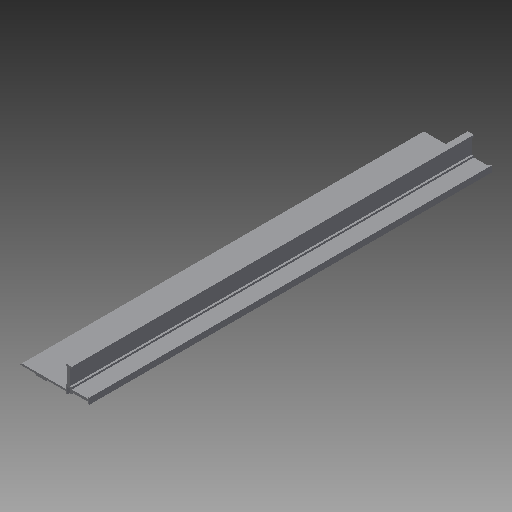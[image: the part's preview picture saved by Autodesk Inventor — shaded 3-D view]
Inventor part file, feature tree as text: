
AUTODESK INVENTOR PART (.ipt)
format: ipt  version: 2018 (Build 220112000, 112)  size: 136,192 bytes
history: native  units: mm
features: other x63, extrude x1, sketch x1
ambient origin geometry x8: Origin, YZ Plane, XZ Plane, XY Plane, X Axis, Y Axis, Z Axis, Center Point
bodies: Solid1 (feature_tree)
feature tree (65):
  extrude  "Extrusion1"  [1 undecoded]
  other  "start_XY"
  other  "start_YZ"
  other  "start_ZX"
  other  "start_X"
  other  "start_Y"
  other  "start_Z"
  other  "start_Center"
  other  "end_XY"
  other  "end_YZ"
  other  "end_ZX"
  other  "end_X"
  other  "end_Y"
  other  "end_Z"
  other  "end_Center"
  other  "side_1a_XY"
  other  "side_1a_YZ"
  other  "side_1a_ZX"
  other  "side_1a_X"
  other  "side_1a_Y"
  other  "side_1a_Z"
  other  "side_1a_Center"
  other  "side_1b_XY"
  other  "side_1b_YZ"
  other  "side_1b_ZX"
  other  "side_1b_X"
  other  "side_1b_Y"
  other  "side_1b_Z"
  other  "side_1b_Center"
  other  "side_1_XY"
  other  "side_1_YZ"
  other  "side_1_ZX"
  other  "side_1_X"
  other  "side_1_Y"
  other  "side_1_Z"
  other  "side_1_Center"
  other  "side_6a_XY"
  other  "side_6a_YZ"
  other  "side_6a_ZX"
  other  "side_6a_X"
  other  "side_6a_Y"
  other  "side_6a_Z"
  other  "side_6a_Center"
  other  "side_2_XY"
  other  "side_2_YZ"
  other  "side_2_ZX"
  other  "side_2_X"
  other  "side_2_Y"
  other  "side_2_Z"
  other  "side_2_Center"
  other  "side_5_XY"
  other  "side_5_YZ"
  other  "side_5_ZX"
  other  "side_5_X"
  other  "side_5_Y"
  other  "side_5_Z"
  other  "side_5_Center"
  other  "side_6_XY"
  other  "side_6_YZ"
  other  "side_6_ZX"
  other  "side_6_X"
  other  "side_6_Y"
  other  "side_6_Z"
  other  "side_6_Center"
  sketch  "Skizze_1"  dims[d0=329.0mm d1=0.0mm]
note: 1 required parameter value undecoded (feature->parameter linkage not recoverable at this tier; creation-order binding heuristic only, values carry confidence <= 0.55)
